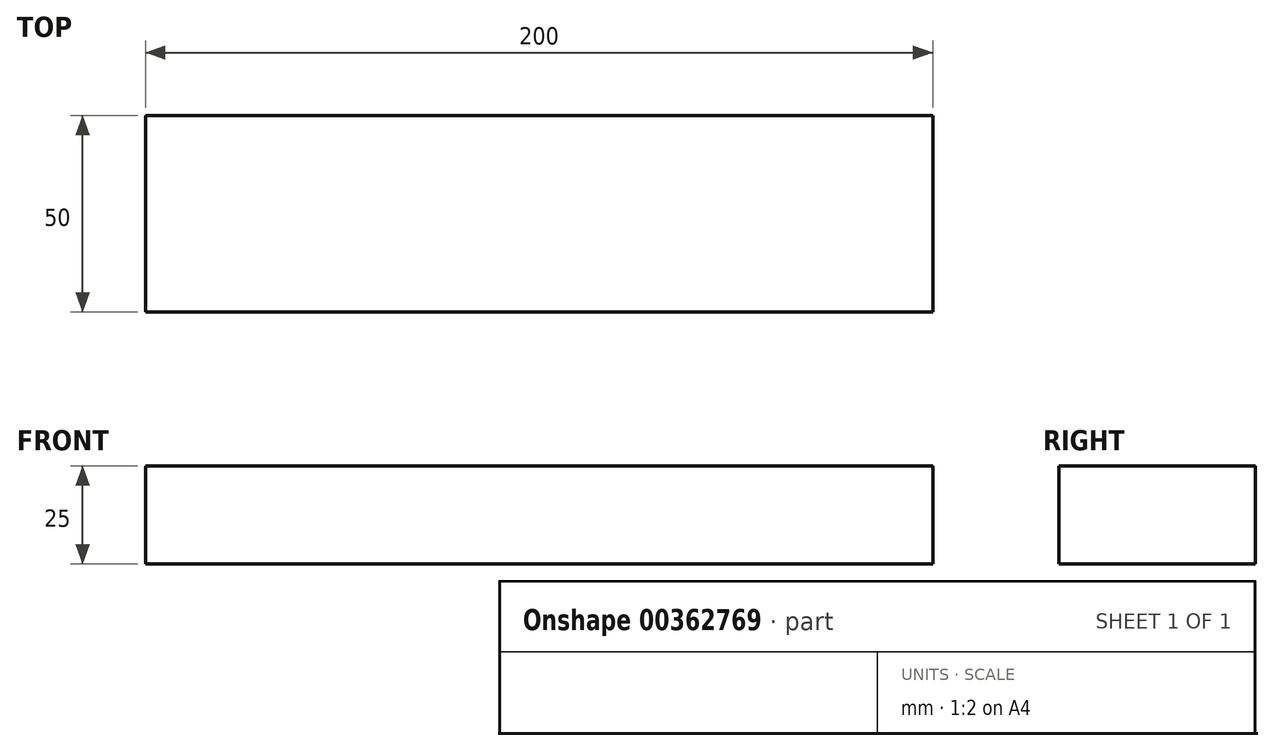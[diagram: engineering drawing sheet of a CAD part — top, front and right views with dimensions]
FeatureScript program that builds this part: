
annotation { "Feature Type Name" : "Feature", "Feature Type Description" : "" }
export const myFeature = defineFeature(function(context is Context, id is Id, definition is map)
    precondition{}
    {
        {
            var Q0;
            Q0=qCreatedBy(makeId("Top.planeOp"),FACE);
            var sketch = newSketch(context, id + "F0", { "sketchPlane" : qUnion([Q0])});
            skLineSegment(sketch, "E0.bottom", {"start": v(0, 0) * mm, "end": v(200, 0) * mm});
            skLineSegment(sketch, "E0.top", {"start": v(0, 50) * mm, "end": v(200, 50) * mm});
            skLineSegment(sketch, "E0.left", {"start": v(0, 0) * mm, "end": v(0, 50) * mm});
            skLineSegment(sketch, "E0.right", {"start": v(200, 0) * mm, "end": v(200, 50) * mm});
            skSolve(sketch);
        }
        {
            var Q0;
            Q0 = qSketchRegion(id + "F0", true);
            extrude(context, id + "F1", {"entities" : qUnion([Q0]), "depth" : 25 * mm});
        }
    });
